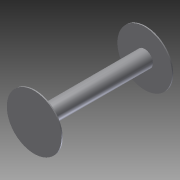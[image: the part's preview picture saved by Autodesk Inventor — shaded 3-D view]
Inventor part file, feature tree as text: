
AUTODESK INVENTOR PART (.ipt)
format: ipt  version: 2012 (Build 160160000, 160)  size: 88,064 bytes
history: native  units: in
note: dims shown in document units (in); Inventor stores cm internally (conversion verified against a paired STEP export)
features: extrude x3, sketch x3
ambient origin geometry x8: Origin, YZ Plane, XZ Plane, XY Plane, X Axis, Y Axis, Z Axis, Center Point
bodies: Solid1 (feature_tree)
feature tree (6):
  extrude  "Extrusion1"  Depth=0.1in TaperAngle=0.0deg
  extrude  "Extrusion2"  Depth=10.0in TaperAngle=0.0deg
  extrude  "Extrusion3"  Depth=0.1in TaperAngle=0.0deg
  sketch  "Sketch1"  dims[d0=5.0in d1=0.1in d2=0.0in]
  sketch  "Sketch2"  dims[d3=1.5in d4=10.0in d5=0.0in]
  sketch  "Sketch3"  dims[d6=5.0in d7=0.1in d8=0.0in]
